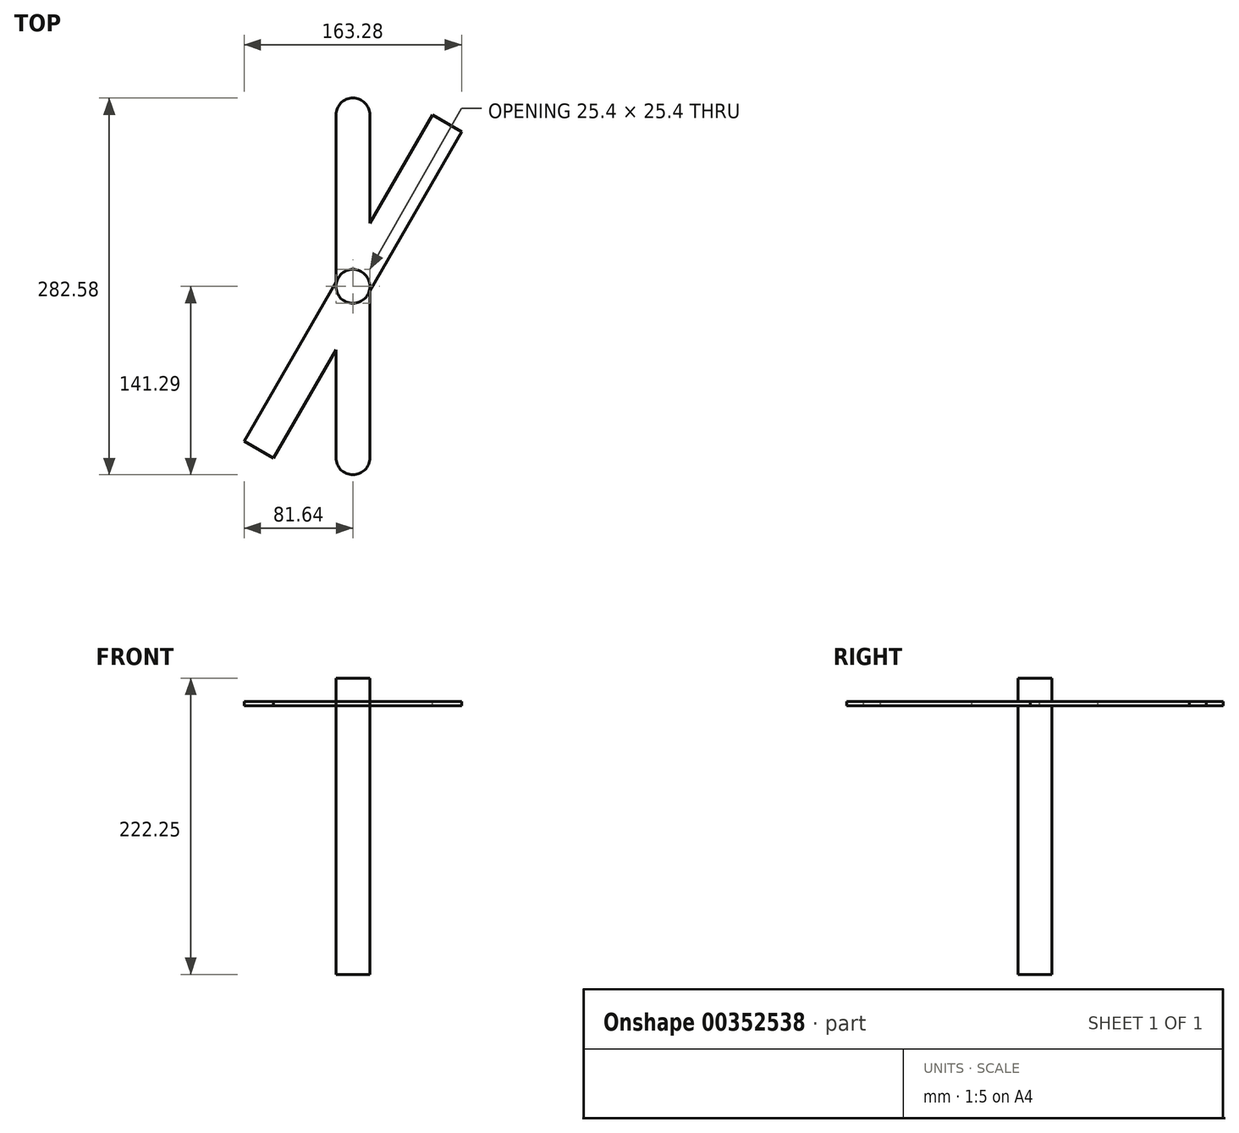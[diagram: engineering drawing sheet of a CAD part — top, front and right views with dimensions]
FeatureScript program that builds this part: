
annotation { "Feature Type Name" : "Feature", "Feature Type Description" : "" }
export const myFeature = defineFeature(function(context is Context, id is Id, definition is map)
    precondition{}
    {
        {
            var Q0;
            Q0=qCreatedBy(makeId("Front.planeOp"),FACE);
            var sketch = newSketch(context, id + "F0", { "sketchPlane" : qUnion([Q0])});
            skLineSegment(sketch, "E0.bottom", {"start": v(-12.7, 94.88) * mm, "end": v(0, 94.88) * mm});
            skLineSegment(sketch, "E0.top", {"start": v(-12.7, -127.37) * mm, "end": v(0, -127.37) * mm});
            skLineSegment(sketch, "E0.left", {"start": v(-12.7, 94.88) * mm, "end": v(-12.7, -127.37) * mm});
            skLineSegment(sketch, "E0.right", {"start": v(0, 94.88) * mm, "end": v(0, -127.37) * mm});
            skSolve(sketch);
        }
        {
            var Q0;
            Q0=makeQuery(id+"F0.imprint","IMPRINT",FACE,{"disambiguationData":[TD([[makeQuery(id+"F0.imprint","IMPRINT",EDGE,{"derivedFrom":sQuery(id+"F0.wireOp",EDGE,"E0.bottom")}),-1.0]])]});
            var Q1;
            Q1=sQuery(id+"F0.wireOp",EDGE,"E0.right");
            revolve(context, id + "F1", {"entities" : qUnion([Q0]), "axis" : qUnion([Q1]), "revolveType" : RevolveType.FULL});
        }
        {
            var Q0;
            Q0=qCreatedBy(makeId("Right.planeOp"),FACE);
            var sketch = newSketch(context, id + "F2", { "sketchPlane" : qUnion([Q0])});
            skLineSegment(sketch, "E1.bottom", {"start": v(12.7, 74.3) * mm, "end": v(-12.7, 74.3) * mm});
            skLineSegment(sketch, "E1.top", {"start": v(12.7, 77.47) * mm, "end": v(-12.7, 77.47) * mm});
            skLineSegment(sketch, "E1.left", {"start": v(12.7, 74.3) * mm, "end": v(12.7, 77.47) * mm});
            skLineSegment(sketch, "E1.right", {"start": v(-12.7, 74.3) * mm, "end": v(-12.7, 77.47) * mm});
            skPoint(sketch, "E1.middle", {"position": v(0, 75.88) * mm});
            skSolve(sketch);
        }
        {
            var Q0;
            Q0=qCreatedBy(makeId("Front.planeOp"),FACE);
            var sketch = newSketch(context, id + "F3", { "sketchPlane" : qUnion([Q0])});
            skLineSegment(sketch, "E2.bottom", {"start": v(12.7, 74.28) * mm, "end": v(-12.7, 74.28) * mm});
            skLineSegment(sketch, "E2.top", {"start": v(12.7, 77.45) * mm, "end": v(-12.7, 77.45) * mm});
            skLineSegment(sketch, "E2.left", {"start": v(12.7, 74.28) * mm, "end": v(12.7, 77.45) * mm});
            skLineSegment(sketch, "E2.right", {"start": v(-12.7, 74.28) * mm, "end": v(-12.7, 77.45) * mm});
            skPoint(sketch, "E2.middle", {"position": v(0, 75.87) * mm});
            skSolve(sketch);
        }
        {
            var Q0;
            Q0 = qSketchRegion(id + "F3", true);
            extrude(context, id + "F4", {"entities" : qUnion([Q0]), "operationType" : NewBodyOperationType.ADD, "endBound" : BoundingType.SYMMETRIC, "depth" : 282.57 * mm});
        }
        {
            var Q0;
            Q0=qCreatedBy(id+"FqyQYq1zeceKhDL_1.planeOp",FACE);
            var sketch = newSketch(context, id + "F5", { "sketchPlane" : qUnion([Q0])});
            skLineSegment(sketch, "E3.bottom", {"start": v(-12.7, 74.3) * mm, "end": v(12.7, 74.3) * mm});
            skLineSegment(sketch, "E3.top", {"start": v(-12.7, 77.47) * mm, "end": v(12.7, 77.47) * mm});
            skLineSegment(sketch, "E3.left", {"start": v(-12.7, 74.3) * mm, "end": v(-12.7, 77.47) * mm});
            skLineSegment(sketch, "E3.right", {"start": v(12.7, 74.3) * mm, "end": v(12.7, 77.47) * mm});
            skPoint(sketch, "E3.middle", {"position": v(0, 75.88) * mm});
            skSolve(sketch);
        }
        {
            var Q0;
            Q0=makeQuery(id+"FrGJp47pIwjt56w_1.opExtrude","CAP_EDGE",EDGE,{"disambiguationData":[OSD([sQuery(id+"F5.wireOp",EDGE,"E3.left")])],"isStart":true});
            var Q1;
            Q1=makeQuery(id+"FrGJp47pIwjt56w_1.opExtrude","CAP_EDGE",EDGE,{"disambiguationData":[OSD([sQuery(id+"F5.wireOp",EDGE,"E3.right")])],"isStart":true});
            var Q2;
            Q2=makeQuery(id+"F2tsKvAxuB83abr_1.opExtrude","CAP_EDGE",EDGE,{"disambiguationData":[OSD([sQuery(id+"F2.wireOp",EDGE,"E1.right")])],"isStart":false});
            var Q3;
            Q3=makeQuery(id+"F2tsKvAxuB83abr_1.opExtrude","CAP_EDGE",EDGE,{"disambiguationData":[OSD([sQuery(id+"F2.wireOp",EDGE,"E1.left")])],"isStart":false});
            var Q4;
            Q4=makeQuery(id+"F4.opExtrude","CAP_EDGE",EDGE,{"disambiguationData":[OSD([sQuery(id+"F3.wireOp",EDGE,"E2.left")])],"isStart":true});
            var Q5;
            Q5=makeQuery(id+"F4.opExtrude","CAP_EDGE",EDGE,{"disambiguationData":[OSD([sQuery(id+"F3.wireOp",EDGE,"E2.right")])],"isStart":true});
            var Q6;
            Q6=makeQuery(id+"FrGJp47pIwjt56w_1.opExtrude","CAP_EDGE",EDGE,{"disambiguationData":[OSD([sQuery(id+"F5.wireOp",EDGE,"E3.left")])],"isStart":false});
            var Q7;
            Q7=makeQuery(id+"F2tsKvAxuB83abr_1.opExtrude","CAP_EDGE",EDGE,{"disambiguationData":[OSD([sQuery(id+"F2.wireOp",EDGE,"E1.left")])],"isStart":true});
            var Q8;
            Q8=makeQuery(id+"FrGJp47pIwjt56w_1.opExtrude","CAP_EDGE",EDGE,{"disambiguationData":[OSD([sQuery(id+"F5.wireOp",EDGE,"E3.right")])],"isStart":false});
            var Q9;
            Q9=makeQuery(id+"F2tsKvAxuB83abr_1.opExtrude","CAP_EDGE",EDGE,{"disambiguationData":[OSD([sQuery(id+"F2.wireOp",EDGE,"E1.right")])],"isStart":true});
            var Q10;
            Q10=makeQuery(id+"F4.opExtrude","CAP_EDGE",EDGE,{"disambiguationData":[OSD([sQuery(id+"F3.wireOp",EDGE,"E2.right")])],"isStart":false});
            var Q11;
            Q11=makeQuery(id+"F4.opExtrude","CAP_EDGE",EDGE,{"disambiguationData":[OSD([sQuery(id+"F3.wireOp",EDGE,"E2.left")])],"isStart":false});
            fillet(context, id + "F6", {"entities" : qUnion([Q0, Q1, Q2, Q3, Q4, Q5, Q6, Q7, Q8, Q9, Q10, Q11]), "radius" : 12.7 * mm, "tangentPropagation" : true, "allowEdgeOverflow" : false});
        }
        {
            var Q0;
            Q0=sQuery(id+"F0.wireOp",EDGE,"E0.right");
            cPlane(context, id + "F7", {"entities" : qUnion([Q0]), "cplaneType" : CPlaneType.LINE_ANGLE, "offset" : 25.4 * mm, "angle" : 120 * degree, "width" : 152.4 * mm, "height" : 152.4 * mm});
        }
        {
            var Q0;
            Q0=qCreatedBy(id+"F7.planeOp",FACE);
            var sketch = newSketch(context, id + "F8", { "sketchPlane" : qUnion([Q0])});
            skLineSegment(sketch, "E4.bottom", {"start": v(-12.7, 74.28) * mm, "end": v(12.7, 74.28) * mm});
            skLineSegment(sketch, "E4.top", {"start": v(-12.7, 77.45) * mm, "end": v(12.7, 77.45) * mm});
            skLineSegment(sketch, "E4.left", {"start": v(-12.7, 74.28) * mm, "end": v(-12.7, 77.45) * mm});
            skLineSegment(sketch, "E4.right", {"start": v(12.7, 74.28) * mm, "end": v(12.7, 77.45) * mm});
            skPoint(sketch, "E4.middle", {"position": v(0, 75.87) * mm});
            skSolve(sketch);
        }
        {
            var Q0;
            Q0 = qSketchRegion(id + "F8", true);
            extrude(context, id + "F9", {"entities" : qUnion([Q0]), "operationType" : NewBodyOperationType.ADD, "endBound" : BoundingType.SYMMETRIC, "depth" : 282.57 * mm});
        }
    });
